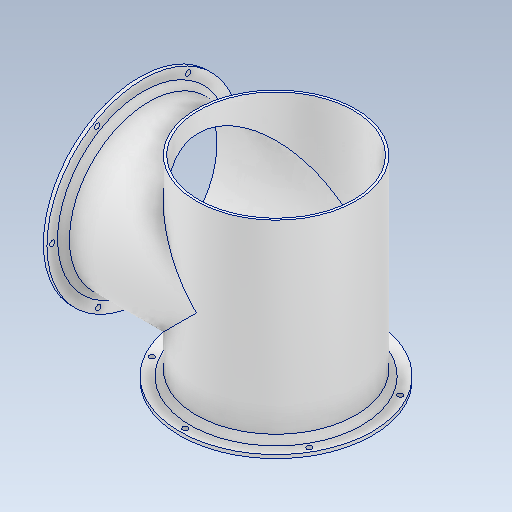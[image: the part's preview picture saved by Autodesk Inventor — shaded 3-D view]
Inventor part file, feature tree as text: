
AUTODESK INVENTOR PART (.ipt)
format: ipt  version: 2021 (Build 250183000, 183)  size: 348,672 bytes
history: native  units: mm
features: sketch x10, extrude x8, revolve x3, hole x3, plane x2, projected_geometry x2, fillet x1
ambient origin geometry x8: Origin, YZ Plane, XZ Plane, XY Plane, X Axis, Y Axis, Z Axis, Center Point
bodies: Solid1 (feature_tree)
feature tree (29):
  revolve  "Revolution1"  [1 undecoded]
  hole  "Hole1"  [1 undecoded]
  fillet  "Fillet1"  [1 undecoded]
  plane  "Work Plane1"
  sketch  "Sketch6"  dims[d10=16.0mm d11=3.0mm]
  extrude  "Extrusion3"  Depth=3.0mm
  extrude  "Extrusion5"  Depth=8.0mm
  extrude  "Extrusion4"  Depth=10.0mm
  revolve  "Revolution2"  [1 undecoded]
  extrude  "Extrusion6"  Depth=165.0mm
  hole  "Hole2"  [1 undecoded]
  extrude  "Extrusion7"  Depth=67.5mm TaperAngle=0.0deg
  plane  "Work Plane2"
  sketch  "Sketch12"  dims[d32=2.0mm d33=5.0mm]
  extrude  "Extrusion9"  Depth=67.5mm
  extrude  "Extrusion10"  TaperAngle=90.0deg  [1 undecoded]
  extrude  "Extrusion11"  Depth=67.5mm
  revolve  "Revolution3"  Angle=45.0deg
  hole  "Hole3"  [1 undecoded]
  sketch  "Sketch2"  dims[d3=90.0deg d5=81.5mm]
  projected_geometry  "Projected Loop1"
  sketch  "Sketch5"  dims[d7=9.0mm d8=5.0mm d9=45.0deg]
  projected_geometry  "Projected Loop6"
  sketch  "Sketch8"  dims[d16=4.5mm d17=8.0mm]
  sketch  "Sketch9"  dims[d18=60.0mm d20=360.0deg]
  sketch  "Sketch11"  dims[d22=4.5mm d23=10.0mm d24=9.4mm d25=2.0mm d26=90.0deg d27=13.0mm d28=20.594885mm d29=4.5mm]
  sketch  "Sketch14"  dims[d34=165.0mm d43=9.0mm]
  sketch  "Sketch15"  dims[d50=135.0mm d51=10.0mm d52=0.0mm]
  sketch  "Sketch16"  dims[d53=112.0mm d54=0.0mm d56=48.0mm d57=0.0mm d59=67.5mm d60=90.0deg d62=5.0mm d63=45.0deg d65=48.0mm d66=0.0mm d67=48.0mm d68=0.0mm d74=2.0mm d75=3.0mm d76=67.5mm d78=2.0mm d79=4.5mm d80=4.5mm d81=60.0mm d83=360.0deg d85=4.5mm d86=6.0mm d87=6.3mm d88=2.0mm d89=90.0deg d90=8.0mm d91=20.594885mm d92=75.0mm d93=135.0mm d95=72.0mm d96=10.0mm d97=0.0mm d98=35.0mm d99=0.0mm d100=2.0mm d101=48.0mm d102=0.0mm d103=9.0mm d105=5.0mm d106=45.0deg d107=3.0mm d109=67.5mm d110=67.5mm d111=90.0deg d112=4.5mm d113=4.5mm d114=60.0mm d116=360.0deg d118=4.5mm d119=6.0mm d120=9.4mm d121=2.0mm d122=90.0deg d123=8.0mm d124=20.594885mm]
note: 7 required parameter values undecoded (feature->parameter linkage not recoverable at this tier; creation-order binding heuristic only, values carry confidence <= 0.55)